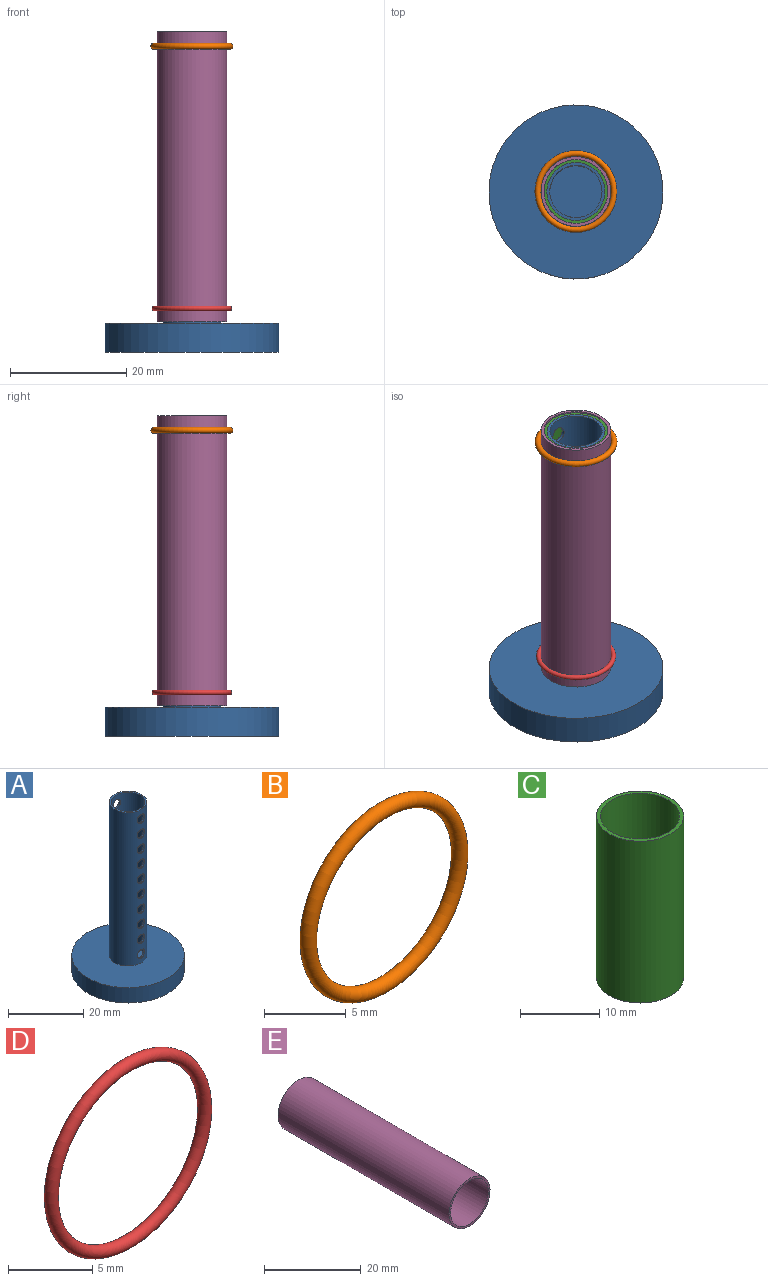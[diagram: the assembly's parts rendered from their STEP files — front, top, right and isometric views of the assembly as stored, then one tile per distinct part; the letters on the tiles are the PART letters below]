
ASSEMBLY  parts=5 mates=4
PART A: 29 faces, bbox 30x30x55 mm
  f0: cylinder r=5mm len=50mm, axis (0,0,-1), area 1443.8mm2, adj f3,f5,f9,f10,f11,f12,f13,f14
  f1: cylinder r=4.5mm len=50.5mm, axis (0,0,-1), area 1300.6mm2, adj f5,f7,f9,f10,f11,f12,f13,f14
  f2: cylinder r=15mm len=30mm, axis (0,0,-1), area 471.2mm2, adj f3,f4
  f3: plane 30x30mm, normal (0,0,1), area 628.3mm2, adj f0,f2
  f4: plane 30x30mm, normal (0,0,-1), area 706.9mm2, adj f2
  f5: plane 10x10mm, normal (0,0,1), area 14.9mm2, adj f0,f1
  f6: cylinder r=14.5mm len=29mm, axis (0,0,-1), area 364.4mm2, adj f7,f8
  f7: plane 29x29mm, normal (0,0,-1), area 596.9mm2, adj f1,f6
  f8: plane 29x29mm, normal (0,0,1), area 660.5mm2, adj f6
  f9: cylinder r=1.41mm len=2.83mm, axis (0,1,0), area 4.5mm2, adj f0,f1
  f10: cylinder r=1.41mm len=2.83mm, axis (0,1,0), area 4.5mm2, adj f0,f1
  f11: cylinder r=1.41mm len=2.83mm, axis (0,1,0), area 4.5mm2, adj f0,f1
  f12: cylinder r=1.41mm len=2.83mm, axis (0,1,0), area 4.5mm2, adj f0,f1
  f13: cylinder r=1.41mm len=2.83mm, axis (0,1,0), area 4.5mm2, adj f0,f1
  f14: cylinder r=1.41mm len=2.83mm, axis (0,1,0), area 4.5mm2, adj f0,f1
  f15: cylinder r=1.41mm len=2.83mm, axis (0,1,0), area 4.5mm2, adj f0,f1
  f16: cylinder r=1.41mm len=2.83mm, axis (0,1,0), area 4.5mm2, adj f0,f1
  f17: cylinder r=1.41mm len=2.83mm, axis (0,1,0), area 4.5mm2, adj f0,f1
  f18: cylinder r=1.41mm len=2.83mm, axis (0,1,0), area 4.5mm2, adj f0,f1
  f19: cylinder r=1.41mm len=2.83mm, axis (0,1,0), area 4.5mm2, adj f0,f1
  f20: cylinder r=1.41mm len=2.83mm, axis (0,1,0), area 4.5mm2, adj f0,f1
  f21: cylinder r=1.41mm len=2.83mm, axis (0,1,0), area 4.5mm2, adj f0,f1
  f22: cylinder r=1.41mm len=2.83mm, axis (0,1,0), area 4.5mm2, adj f0,f1
  f23: cylinder r=1.41mm len=2.83mm, axis (0,1,0), area 4.5mm2, adj f0,f1
  f24: cylinder r=1.41mm len=2.83mm, axis (0,1,0), area 4.5mm2, adj f0,f1
  f25: cylinder r=1.41mm len=2.83mm, axis (0,1,0), area 4.5mm2, adj f0,f1
  f26: cylinder r=1.41mm len=2.83mm, axis (0,1,0), area 4.5mm2, adj f0,f1
  f27: cylinder r=1.41mm len=2.83mm, axis (0,1,0), area 4.5mm2, adj f0,f1
  f28: cylinder r=1.41mm len=2.83mm, axis (0,1,0), area 4.5mm2, adj f0,f1
PART B: 1 faces, bbox 15.3x1x15.3 mm
  f0: torus R=6.56mm, axis (0,1,0), area 131.9mm2
PART C: 4 faces, bbox 11x11x25 mm
  f0: cylinder r=5mm len=25mm, axis (0,0,-1), area 785.4mm2, adj f2,f3
  f1: cylinder r=5.5mm len=25mm, axis (0,0,-1), area 863.9mm2, adj f2,f3
  f2: plane 11x11mm, normal (0,0,1), area 16.5mm2, adj f0,f1
  f3: plane 11x11mm, normal (0,0,-1), area 16.5mm2, adj f0,f1
PART D: 1 faces, bbox 14.8x0.8x14.8 mm
  f0: torus R=6.44mm, axis (0,1,0), area 106.4mm2
PART E: 4 faces, bbox 12x50x12 mm
  f0: cylinder r=5.5mm len=50mm, axis (0,1,0), area 1727.9mm2, adj f2,f3
  f1: cylinder r=6mm len=50mm, axis (0,1,0), area 1885mm2, adj f2,f3
  f2: plane 12x12mm, normal (0,-1,0), area 18.1mm2, adj f0,f1
  f3: plane 12x12mm, normal (0,1,0), area 18.1mm2, adj f0,f1
PLACE A t=(-9.11,8.71,3.52)mm fixed
PLACE B rot(axis=(-1,0,0),90deg) t=(-9.11,8.71,54.87)mm
PLACE C t=(-9.11,8.71,33.52)mm
PLACE D rot(axis=(-1,0,0),90deg) t=(-9.11,8.71,-38.01)mm
PLACE E rot(axis=(-1,0,0),90deg) t=(-9.11,8.71,8.76)mm
MATE slider B.f0 <-> E.f1  axis (0,0,-1) through (-9.11,8.71,56.27)mm
MATE slider E.f1 <-> C.f1  axis (0,0,-1) through (-9.11,8.71,33.76)mm
MATE slider D.f0 <-> E.f1  axis (0,0,-1) through (-9.11,8.71,11.06)mm
MATE slider C.f1 <-> A.f0  axis (0,0,1) through (-9.11,8.71,58.52)mm
